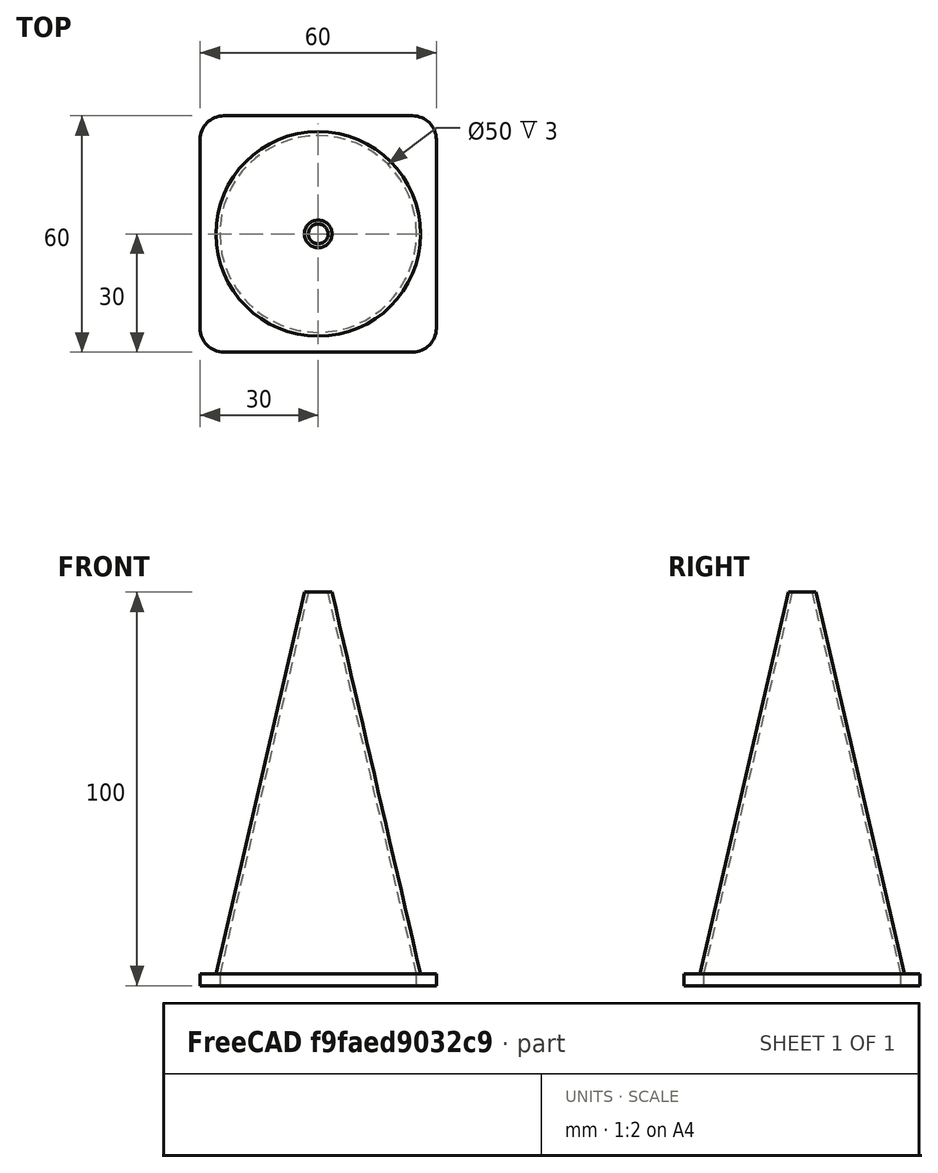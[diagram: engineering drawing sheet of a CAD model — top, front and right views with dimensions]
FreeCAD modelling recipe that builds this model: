
FCSTD DOCUMENT  (FreeCAD 0.18R16146 (Git))
Label: training-cone
License: All rights reserved
LicenseURL: http://en.wikipedia.org/wiki/All_rights_reserved
objects: TechDraw::DrawViewDimension×4, Sketcher::SketchObject×3, TechDraw::DrawViewPart×3, PartDesign::Plane×2, PartDesign::Pad×1, Spreadsheet::Sheet×1, PartDesign::AdditiveLoft×1, PartDesign::Fillet×1, PartDesign::Body×1, TechDraw::DrawSVGTemplate×1, TechDraw::DrawPage×1
note: 11 computed .brp shape members not serialized (recipe doc carries the construction recipe); baked Part::Feature solids carry a one-line shape summary decoded from their .brp

FEATURE [Sketcher::SketchObject] Sketch  label="base_sketch"
  MapMode = 5
  Support = -> [XY_Plane]
  expr: Constraints[12] = p.inner_base_circle_diameter
  expr: Constraints[11] = p.base_width
  sketch-geometry (5):
    g0: LineSegment StartX=-30 StartY=30 StartZ=0 EndX=30 EndY=30 EndZ=0
    g1: LineSegment StartX=30 StartY=30 StartZ=0 EndX=30 EndY=-30 EndZ=0
    g2: LineSegment StartX=30 StartY=-30 StartZ=0 EndX=-30 EndY=-30 EndZ=0
    g3: LineSegment StartX=-30 StartY=-30 StartZ=0 EndX=-30 EndY=30 EndZ=0
    g4: Circle CenterX=1e-16 CenterY=0 CenterZ=0 NormalX=0 NormalY=0 NormalZ=1 AngleXU=0 Radius=25
  constraints (13):
    c: Coincident(g0,g1)
    c: Coincident(g1,g2)
    c: Coincident(g2,g3)
    c: Coincident(g3,g0)
    c: Horizontal(g0)
    c: Horizontal(g2)
    c: Vertical(g1)
    c: Vertical(g3)
    c: Coincident(g4,g-1)
    c: Equal(g2,g3)
    c: Symmetric(g2,g0,g4)
    c: Distance(g2) = 60
    c: Diameter(g4) = 50
FEATURE [PartDesign::Pad] Pad  label="base_pad"
  Length = 3
  Length2 = 100
  Profile = -> Sketch
  Type = 0
  expr: Length = p.base_height
FEATURE [Spreadsheet::Sheet] Spreadsheet  label="p"
  cells = A1=base_width; B1(base_width)==60mm; A2=base_height; B2(base_height)==3mm; A3=cone_thickness; B3(cone_thickness)==2mm; A4=cone_height; B4(cone_height)==100mm; A5=inner_base_circle_diameter; B5(inner_base_circle_diameter)==base_width - 10mm; A6=outer_base_circle_diameter; B6(outer_base_circle_diameter)==inner_base_circle_diameter + cone_thickness; A7=inner_top_circle_diameter; B7(inner_top_circle_diameter)==5mm; A8=outer_top_circle_diameter; B8(outer_top_circle_diameter)==inner_top_circle_diameter + cone_thickness
FEATURE [PartDesign::Plane] DatumPlane  label="loft_bottom_plane"
  AttachmentOffset = pos=(0,0,3) rot=(0,0,1;0rad)
  Length = 72
  MapMode = 5
  Placement = pos=(0,0,3) rot=(0,0,1;0rad)
  ResizeMode = 0
  Support = -> [XY_Plane]
  Width = 72
  expr: AttachmentOffset.Base.z = p.base_height
FEATURE [PartDesign::Plane] DatumPlane001  label="loft_top_plane"
  AttachmentOffset = pos=(0,0,100) rot=(0,0,1;0rad)
  Length = 72
  MapMode = 5
  Placement = pos=(0,0,100) rot=(0,0,1;0rad)
  ResizeMode = 0
  Support = -> [XY_Plane]
  Width = 72
  expr: AttachmentOffset.Base.z = p.cone_height
FEATURE [Sketcher::SketchObject] Sketch001  label="bottom_loft_sketch"
  MapMode = 5
  Placement = pos=(0,0,3) rot=(0,0,1;0rad)
  Support = -> [DatumPlane]
  expr: Constraints[2] = p.outer_base_circle_diameter
  expr: Constraints[1] = p.inner_base_circle_diameter
  sketch-geometry (2):
    g0: Circle CenterX=0 CenterY=0 CenterZ=0 NormalX=0 NormalY=0 NormalZ=1 AngleXU=0 Radius=25
    g1: Circle CenterX=0 CenterY=0 CenterZ=0 NormalX=0 NormalY=0 NormalZ=1 AngleXU=0 Radius=26
  constraints (3):
    c: Coincident(g1,g0)
    c: Diameter(g0) = 50
    c: Diameter(g1) = 52
FEATURE [Sketcher::SketchObject] Sketch002  label="top_loft_sketch"
  MapMode = 5
  Placement = pos=(0,0,100) rot=(0,0,1;0rad)
  Support = -> [DatumPlane001]
  expr: Constraints[3] = p.outer_top_circle_diameter
  expr: Constraints[2] = p.inner_top_circle_diameter
  sketch-geometry (2):
    g0: Circle CenterX=0 CenterY=0 CenterZ=0 NormalX=0 NormalY=0 NormalZ=1 AngleXU=0 Radius=2.5
    g1: Circle CenterX=0 CenterY=0 CenterZ=0 NormalX=0 NormalY=0 NormalZ=1 AngleXU=0 Radius=3.5
  constraints (4):
    c: Coincident(g0,g-1)
    c: Coincident(g1,g0)
    c: Diameter(g0) = 5
    c: Diameter(g1) = 7
FEATURE [PartDesign::AdditiveLoft] AdditiveLoft
  BaseFeature = -> Pad
  Closed = false
  Profile = -> Sketch001
  Ruled = false
  Sections = -> [Sketch002]
FEATURE [PartDesign::Fillet] Fillet
  Base = -> AdditiveLoft [Edge5,Edge8,Edge1,Edge2]
  BaseFeature = -> AdditiveLoft
  Radius = 6
FEATURE [PartDesign::Body] Body
  Group = -> [Sketch,Pad,DatumPlane,DatumPlane001,Sketch001,Sketch002,AdditiveLoft,Fillet]
  Origin = -> Origin
  Tip = -> Fillet
FEATURE [TechDraw::DrawSVGTemplate] Template
  EditableTexts = CompanyAddress=Beirut Lebanon; CompanyName=Kanj Workshop; DrawingNumber=1.0; DrawingTitle1=mini basketball training cone; DrawnBy=Hassan Kanj
  Height = 215.9
  Orientation = 1
  Width = 279.4
FEATURE [TechDraw::DrawViewPart] View
  CoarseView = false
  Direction = (0.577,-0.577,0.577)
  Focus = 100
  HardHidden = false
  IsoCount = 0
  IsoHidden = false
  IsoVisible = false
  LockPosition = false
  Perspective = false
  Rotation = 0
  ScaleType = 0
  SeamHidden = false
  SeamVisible = false
  SmoothHidden = false
  SmoothVisible = false
  Source = -> [Body]
  X = 176.561
  Y = 138.667
FEATURE [TechDraw::DrawViewPart] View001
  CoarseView = false
  Direction = (0,0,1)
  Focus = 100
  HardHidden = false
  IsoCount = 0
  IsoHidden = false
  IsoVisible = false
  LockPosition = false
  Perspective = false
  Rotation = 0
  ScaleType = 0
  SeamHidden = false
  SeamVisible = false
  SmoothHidden = false
  SmoothVisible = false
  Source = -> [Body]
  X = 66.4169
  Y = 53.5362
FEATURE [TechDraw::DrawViewPart] View002
  CoarseView = false
  Direction = (1,0,0)
  Focus = 100
  HardHidden = false
  IsoCount = 0
  IsoHidden = false
  IsoVisible = false
  LockPosition = false
  Perspective = false
  Rotation = 0
  ScaleType = 0
  SeamHidden = false
  SeamVisible = false
  SmoothHidden = false
  SmoothVisible = false
  Source = -> [Body]
  X = 67.2945
  Y = 144.811
FEATURE [TechDraw::DrawViewDimension] Dimension
  Arbitrary = false
  FormatSpec = %.2f
  LockPosition = false
  MeasureType = 1
  OverTolerance = 0
  References2D = -> [View]
  Rotation = 0
  ScaleType = 0
  Type = 0
  UnderTolerance = 0
  X = -23.0385
  Y = -46.0672
FEATURE [TechDraw::DrawViewDimension] Dimension001
  Arbitrary = false
  FormatSpec = %.2f
  LockPosition = false
  MeasureType = 1
  OverTolerance = 0
  References2D = -> [View]
  Rotation = 0
  ScaleType = 0
  Type = 0
  UnderTolerance = 0
  X = 32.1138
  Y = -44.7508
FEATURE [TechDraw::DrawViewDimension] Dimension002
  Arbitrary = false
  FormatSpec = ⌀%.2f
  LockPosition = false
  MeasureType = 1
  OverTolerance = 0
  References2D = -> [View001]
  Rotation = 0
  ScaleType = 0
  Type = 5
  UnderTolerance = 0
  X = 1.75528
  Y = 16.6752
FEATURE [TechDraw::DrawViewDimension] Dimension003
  Arbitrary = false
  FormatSpec = %.2f
  LockPosition = false
  MeasureType = 1
  OverTolerance = 0
  References2D = -> [View002]
  Rotation = 0
  ScaleType = 0
  Type = 2
  UnderTolerance = 0
  X = 40.6404
  Y = 1.93882
FEATURE [TechDraw::DrawPage] Page
  KeepUpdated = true
  ProjectionType = 0
  Template = -> Template
  Views = -> [View,View001,View002,Dimension,Dimension001,Dimension002,Dimension003]
